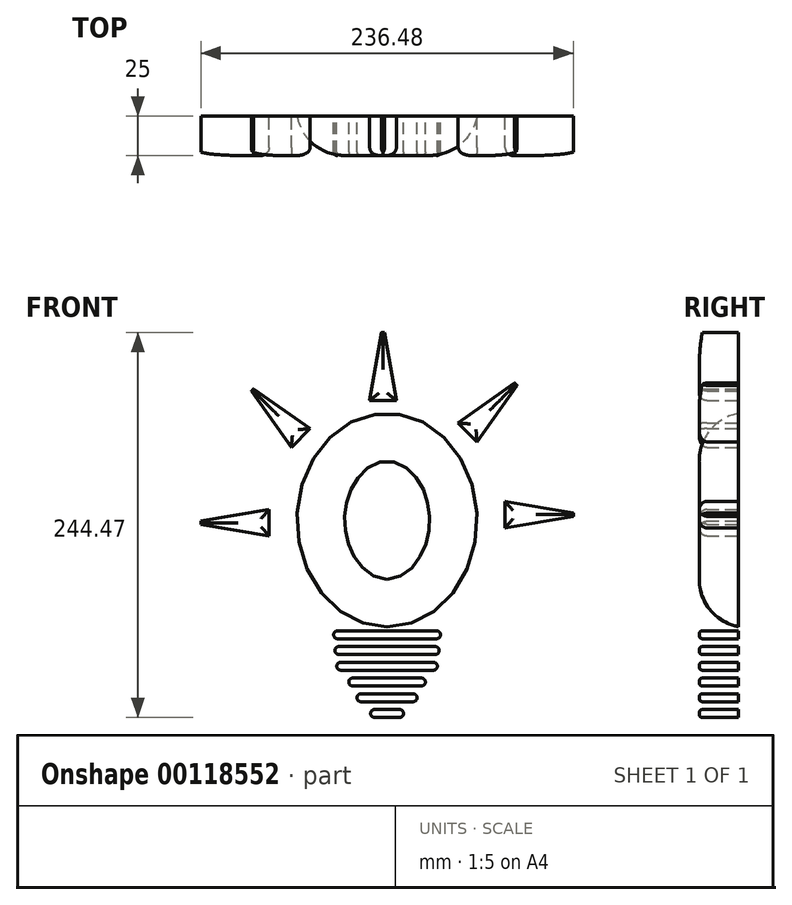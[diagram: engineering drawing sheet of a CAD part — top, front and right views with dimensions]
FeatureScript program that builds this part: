
annotation { "Feature Type Name" : "Feature", "Feature Type Description" : "" }
export const myFeature = defineFeature(function(context is Context, id is Id, definition is map)
    precondition{}
    {
        {
            var Q0;
            Q0=qCreatedBy(makeId("Front.planeOp"),FACE);
            var sketch = newSketch(context, id + "F0", { "sketchPlane" : qUnion([Q0])});
            skEllipse(sketch, "E0", {"center": v(0, 34.87) * mm, "majorRadius": 67.76 * mm, "minorRadius": 57.17 * mm, "majorAxis": v(0, -1)});
            skSolve(sketch);
        }
        {
            var Q0;
            Q0 = qSketchRegion(id + "FFalVhq41jpC5tf_1", true);
            var Q1;
            Q1=makeQuery(id+"F0.imprint","IMPRINT",FACE,{"disambiguationData":[TD([[makeQuery(id+"F0.imprint","IMPRINT",EDGE,{"derivedFrom":sQuery(id+"F0.wireOp",EDGE,"E0")}),1.0]])]});
            extrude(context, id + "F1", {"entities" : qUnion([Q0, Q1]), "depth" : 25 * mm});
        }
        {
            var Q0;
            Q0=makeQuery(id+"F1.opExtrude","CAP_EDGE",EDGE,{"disambiguationData":[OSD([sQuery(id+"F0.wireOp",EDGE,"E0")])],"isStart":false});
            fillet(context, id + "F2", {"entities" : qUnion([Q0]), "radius" : 30.73 * mm, "tangentPropagation" : true, "allowEdgeOverflow" : false});
        }
        {
            var Q0;
            Q0=qCreatedBy(makeId("Front.planeOp"),FACE);
            var sketch = newSketch(context, id + "F3", { "sketchPlane" : qUnion([Q0])});
            skLineSegment(sketch, "E1", {"start": v(0, 0) * mm, "end": v(0, -107.04) * mm, "construction": true});
            skLineSegment(sketch, "E2", {"start": v(-29.45, -58) * mm, "end": v(29.45, -58) * mm});
            skLineSegment(sketch, "E3", {"start": v(-21.82, -68) * mm, "end": v(21.82, -68) * mm});
            skLineSegment(sketch, "E4", {"start": v(-16.6, -78) * mm, "end": v(16.6, -78) * mm});
            skLineSegment(sketch, "E5", {"start": v(-30.61, -48) * mm, "end": v(30.61, -48) * mm});
            skLineSegment(sketch, "E6", {"start": v(-31.45, -38) * mm, "end": v(31.45, -38) * mm});
            skLineSegment(sketch, "E7", {"start": v(-7.96, -88) * mm, "end": v(7.96, -88) * mm});
            skArc(sketch, "E8.0.startCap", {"start": v(-31.45, -40.5) * mm, "mid": v(-33.95, -38) * mm, "end": v(-31.45, -35.5) * mm});
            skArc(sketch, "E8.0.endCap", {"start": v(31.45, -35.5) * mm, "mid": v(33.95, -38) * mm, "end": v(31.45, -40.5) * mm});
            skLineSegment(sketch, "E8.0.left", {"start": v(-31.45, -35.5) * mm, "end": v(31.45, -35.5) * mm});
            skLineSegment(sketch, "E8.0.right", {"start": v(-31.45, -40.5) * mm, "end": v(31.45, -40.5) * mm});
            skArc(sketch, "E8.1.startCap", {"start": v(-30.61, -50.5) * mm, "mid": v(-33.11, -48) * mm, "end": v(-30.61, -45.5) * mm});
            skArc(sketch, "E8.1.endCap", {"start": v(30.61, -45.5) * mm, "mid": v(33.11, -48) * mm, "end": v(30.61, -50.5) * mm});
            skLineSegment(sketch, "E8.1.left", {"start": v(-30.61, -45.5) * mm, "end": v(30.61, -45.5) * mm});
            skLineSegment(sketch, "E8.1.right", {"start": v(-30.61, -50.5) * mm, "end": v(30.61, -50.5) * mm});
            skArc(sketch, "E8.2.startCap", {"start": v(-29.45, -60.5) * mm, "mid": v(-31.95, -58) * mm, "end": v(-29.45, -55.5) * mm});
            skArc(sketch, "E8.2.endCap", {"start": v(29.45, -55.5) * mm, "mid": v(31.95, -58) * mm, "end": v(29.45, -60.5) * mm});
            skLineSegment(sketch, "E8.2.left", {"start": v(-29.45, -55.5) * mm, "end": v(29.45, -55.5) * mm});
            skLineSegment(sketch, "E8.2.right", {"start": v(-29.45, -60.5) * mm, "end": v(29.45, -60.5) * mm});
            skArc(sketch, "E8.3.startCap", {"start": v(-21.82, -70.5) * mm, "mid": v(-24.32, -68) * mm, "end": v(-21.82, -65.5) * mm});
            skArc(sketch, "E8.3.endCap", {"start": v(21.82, -65.5) * mm, "mid": v(24.32, -68) * mm, "end": v(21.82, -70.5) * mm});
            skLineSegment(sketch, "E8.3.left", {"start": v(-21.82, -65.5) * mm, "end": v(21.82, -65.5) * mm});
            skLineSegment(sketch, "E8.3.right", {"start": v(-21.82, -70.5) * mm, "end": v(21.82, -70.5) * mm});
            skArc(sketch, "E8.4.startCap", {"start": v(-16.6, -80.5) * mm, "mid": v(-19.1, -78) * mm, "end": v(-16.6, -75.5) * mm});
            skArc(sketch, "E8.4.endCap", {"start": v(16.6, -75.5) * mm, "mid": v(19.1, -78) * mm, "end": v(16.6, -80.5) * mm});
            skLineSegment(sketch, "E8.4.left", {"start": v(-16.6, -75.5) * mm, "end": v(16.6, -75.5) * mm});
            skLineSegment(sketch, "E8.4.right", {"start": v(-16.6, -80.5) * mm, "end": v(16.6, -80.5) * mm});
            skArc(sketch, "E8.5.startCap", {"start": v(-7.96, -90.5) * mm, "mid": v(-10.46, -88) * mm, "end": v(-7.96, -85.5) * mm});
            skArc(sketch, "E8.5.endCap", {"start": v(7.96, -85.5) * mm, "mid": v(10.46, -88) * mm, "end": v(7.96, -90.5) * mm});
            skLineSegment(sketch, "E8.5.left", {"start": v(-7.96, -85.5) * mm, "end": v(7.96, -85.5) * mm});
            skLineSegment(sketch, "E8.5.right", {"start": v(-7.96, -90.5) * mm, "end": v(7.96, -90.5) * mm});
            skSolve(sketch);
        }
        {
            var Q0;
            Q0 = qSketchRegion(id + "F3", true);
            extrude(context, id + "F4", {"entities" : qUnion([Q0]), "depth" : 25 * mm});
        }
        {
            var Q0;
            Q0=makeQuery(id+"F4.opExtrude","CAP_FACE",FACE,{"disambiguationData":[OSD([sQuery(id+"F3.wireOp",EDGE,"E8.0.startCap"),sQuery(id+"F3.wireOp",EDGE,"E8.0.endCap"),sQuery(id+"F3.wireOp",EDGE,"E8.0.left"),sQuery(id+"F3.wireOp",EDGE,"E8.0.right")])],"isStart":false});
            var Q1;
            Q1=makeQuery(id+"F4.opExtrude","CAP_FACE",FACE,{"disambiguationData":[OSD([sQuery(id+"F3.wireOp",EDGE,"E8.1.startCap"),sQuery(id+"F3.wireOp",EDGE,"E8.1.endCap"),sQuery(id+"F3.wireOp",EDGE,"E8.1.left"),sQuery(id+"F3.wireOp",EDGE,"E8.1.right")])],"isStart":false});
            var Q2;
            Q2=makeQuery(id+"F4.opExtrude","CAP_FACE",FACE,{"disambiguationData":[OSD([sQuery(id+"F3.wireOp",EDGE,"E8.2.startCap"),sQuery(id+"F3.wireOp",EDGE,"E8.2.endCap"),sQuery(id+"F3.wireOp",EDGE,"E8.2.left"),sQuery(id+"F3.wireOp",EDGE,"E8.2.right")])],"isStart":false});
            var Q3;
            Q3=makeQuery(id+"F4.opExtrude","CAP_FACE",FACE,{"disambiguationData":[OSD([sQuery(id+"F3.wireOp",EDGE,"E8.3.startCap"),sQuery(id+"F3.wireOp",EDGE,"E8.3.endCap"),sQuery(id+"F3.wireOp",EDGE,"E8.3.left"),sQuery(id+"F3.wireOp",EDGE,"E8.3.right")])],"isStart":false});
            var Q4;
            Q4=makeQuery(id+"F4.opExtrude","CAP_FACE",FACE,{"disambiguationData":[OSD([sQuery(id+"F3.wireOp",EDGE,"E8.4.startCap"),sQuery(id+"F3.wireOp",EDGE,"E8.4.endCap"),sQuery(id+"F3.wireOp",EDGE,"E8.4.left"),sQuery(id+"F3.wireOp",EDGE,"E8.4.right")])],"isStart":false});
            var Q5;
            Q5=makeQuery(id+"F4.opExtrude","CAP_FACE",FACE,{"disambiguationData":[OSD([sQuery(id+"F3.wireOp",EDGE,"E8.5.startCap"),sQuery(id+"F3.wireOp",EDGE,"E8.5.endCap"),sQuery(id+"F3.wireOp",EDGE,"E8.5.left"),sQuery(id+"F3.wireOp",EDGE,"E8.5.right")])],"isStart":false});
            fillet(context, id + "F5", {"entities" : qUnion([Q0, Q1, Q2, Q3, Q4, Q5]), "radius" : 2 * mm, "tangentPropagation" : true, "allowEdgeOverflow" : false});
        }
        {
            var Q0;
            Q0=qCreatedBy(makeId("Front.planeOp"),FACE);
            var sketch = newSketch(context, id + "F6", { "sketchPlane" : qUnion([Q0])});
            skCircle(sketch, "E9", {"center": v(0, 35.73) * mm, "radius": 79.73 * mm, "construction": true});
            skSolve(sketch);
        }
        {
            var Q0;
            Q0=qCreatedBy(makeId("Front.planeOp"),FACE);
            var sketch = newSketch(context, id + "F7", { "sketchPlane" : qUnion([Q0])});
            skLineSegment(sketch, "E10.right", {"start": v(-118.24, 32.17) * mm, "end": v(-118.24, 34.17) * mm});
            skLineSegment(sketch, "E11", {"start": v(-102.03, 33.17) * mm, "end": v(-74.96, 33.17) * mm, "construction": true});
            skPoint(sketch, "E11.startSnap0", {"position": v(-118.24, 33.17) * mm});
            skLineSegment(sketch, "E12", {"start": v(-118.24, 34.17) * mm, "end": v(-74.96, 41.65) * mm});
            skLineSegment(sketch, "E13.MirrorCS", {"start": v(-118.24, 32.17) * mm, "end": v(-74.96, 24.7) * mm});
            skLineSegment(sketch, "E14", {"start": v(-74.96, 41.65) * mm, "end": v(-74.96, 24.7) * mm});
            skSolve(sketch);
        }
        {
            var Q0;
            Q0 = qSketchRegion(id + "F7", true);
            extrude(context, id + "F8", {"entities" : qUnion([Q0]), "depth" : 25 * mm});
        }
        {
            var Q0;
            Q0=makeQuery(id+"F8.opExtrude","CAP_FACE",FACE,{"disambiguationData":[OSD([sQuery(id+"F7.wireOp",EDGE,"E10.right"),sQuery(id+"F7.wireOp",EDGE,"E12"),sQuery(id+"F7.wireOp",EDGE,"E13.MirrorCS"),sQuery(id+"F7.wireOp",EDGE,"E14")])],"isStart":false});
            fillet(context, id + "F9", {"entities" : qUnion([Q0]), "radius" : 5 * mm, "tangentPropagation" : true, "allowEdgeOverflow" : false});
        }
        {
            var Q0;
            Q0=makeQuery(id+"F8.opExtrude","SWEPT_BODY",BODY,{"disambiguationData":[OSD([sQuery(id+"F7.wireOp",EDGE,"E10.right"),sQuery(id+"F7.wireOp",EDGE,"E12"),sQuery(id+"F7.wireOp",EDGE,"E13.MirrorCS"),sQuery(id+"F7.wireOp",EDGE,"E14")])]});
            var Q1;
            Q1=sQuery(id+"F6.wireOp",EDGE,"E9");
            circularPattern(context, id + "F10", {"entities" : qUnion([Q0]), "axis" : qUnion([Q1]), "angle" : 45 * degree, "instanceCount" : 5, "oppositeDirection" : true});
        }
    });
